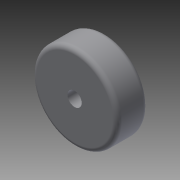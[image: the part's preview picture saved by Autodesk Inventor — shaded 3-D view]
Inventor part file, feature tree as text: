
AUTODESK INVENTOR PART (.ipt)
format: ipt  version: 2013 (Build 170138000, 138)  size: 108,544 bytes
history: native  units: in
note: dims shown in document units (in); Inventor stores cm internally (conversion verified against a paired STEP export)
features: extrude x2, sketch x2, fillet x1
ambient origin geometry x8: Origin, YZ Plane, XZ Plane, XY Plane, X Axis, Y Axis, Z Axis, Center Point
bodies: Solid1 (feature_tree)
feature tree (5):
  extrude  "Extrusion1"  Depth=0.8125in TaperAngle=0.0deg
  extrude  "Extrusion2"  Depth=0.5in TaperAngle=0.0deg
  fillet  "Fillet1"  Radius=0.125in
  sketch  "Sketch1"  dims[d0=2.25in d1=0.8125in d2=0.0in]
  sketch  "Sketch2"  dims[d3=0.375in d4=0.5in d5=0.0in d6=0.125in]
